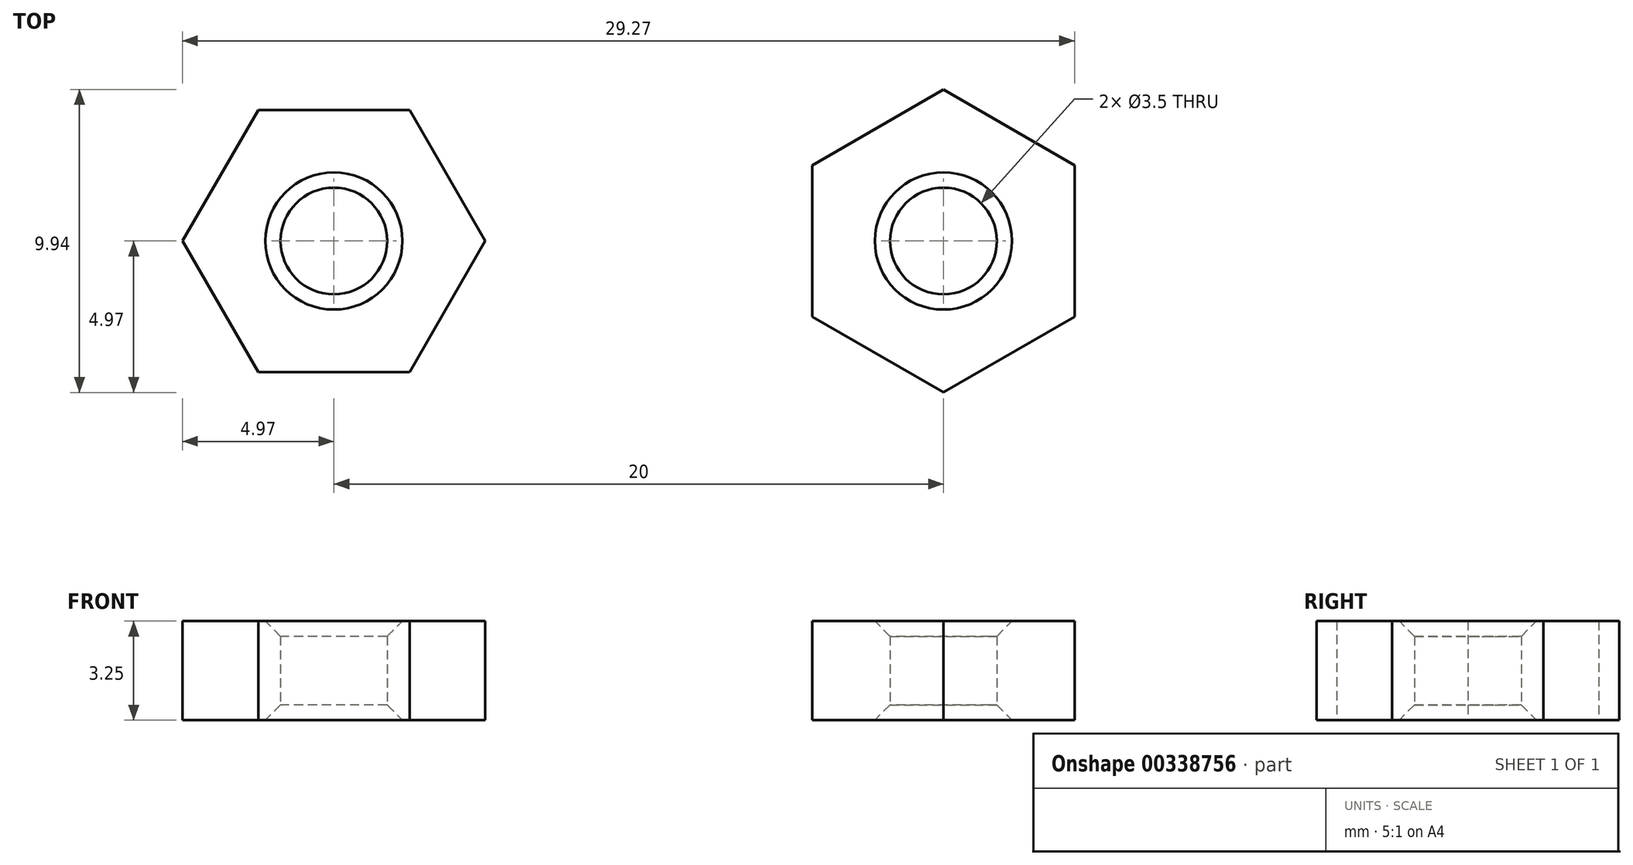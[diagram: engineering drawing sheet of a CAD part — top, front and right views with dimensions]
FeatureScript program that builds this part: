
annotation { "Feature Type Name" : "Feature", "Feature Type Description" : "" }
export const myFeature = defineFeature(function(context is Context, id is Id, definition is map)
    precondition{}
    {
        {
            var Q0;
            Q0=qCreatedBy(makeId("Top.planeOp"),FACE);
            var sketch = newSketch(context, id + "F0", { "sketchPlane" : qUnion([Q0])});
            skCircle(sketch, "E0.cCircle", {"center": v(0, 0) * mm, "radius": 4.3 * mm, "construction": true});
            skLineSegment(sketch, "E0.0", {"start": v(-2.48, 4.3) * mm, "end": v(2.48, 4.3) * mm});
            skLineSegment(sketch, "E0.1", {"start": v(2.48, 4.3) * mm, "end": v(4.97, 0) * mm});
            skLineSegment(sketch, "E0.2", {"start": v(4.97, 0) * mm, "end": v(2.48, -4.3) * mm});
            skLineSegment(sketch, "E0.3", {"start": v(2.48, -4.3) * mm, "end": v(-2.48, -4.3) * mm});
            skLineSegment(sketch, "E0.4", {"start": v(-2.48, -4.3) * mm, "end": v(-4.97, 0) * mm});
            skLineSegment(sketch, "E0.5", {"start": v(-4.97, 0) * mm, "end": v(-2.48, 4.3) * mm});
            skPoint(sketch, "E0.0.midPoint", {"position": v(0, 4.3) * mm});
            skCircle(sketch, "E1", {"center": v(0, 0) * mm, "radius": 1.75 * mm});
            skSolve(sketch);
        }
        {
            var Q0;
            Q0=makeQuery(id+"F0.imprint","IMPRINT",FACE,{"disambiguationData":[TD([[makeQuery(id+"F0.imprint","IMPRINT",EDGE,{"derivedFrom":sQuery(id+"F0.wireOp",EDGE,"E0.0")}),-1.0]])]});
            extrude(context, id + "F1", {"entities" : qUnion([Q0]), "depth" : 3.25 * mm});
        }
        {
            var Q0;
            Q0=makeQuery(id+"F1.opExtrude","CAP_EDGE",EDGE,{"disambiguationData":[OSD([sQuery(id+"F0.wireOp",EDGE,"E1")])],"isStart":false});
            var Q1;
            Q1=makeQuery(id+"F1.opExtrude","CAP_EDGE",EDGE,{"disambiguationData":[OSD([sQuery(id+"F0.wireOp",EDGE,"E1")])],"isStart":true});
            chamfer(context, id + "F2", {"entities" : qUnion([Q0, Q1]), "width" : .5 * mm, "tangentPropagation" : true});
        }
        {
            var Q0;
            Q0=makeQuery(id+"F1.opExtrude","SWEPT_BODY",BODY,{"disambiguationData":[OSD([sQuery(id+"F0.wireOp",EDGE,"E0.0"),sQuery(id+"F0.wireOp",EDGE,"E0.1"),sQuery(id+"F0.wireOp",EDGE,"E0.2"),sQuery(id+"F0.wireOp",EDGE,"E0.3"),sQuery(id+"F0.wireOp",EDGE,"E0.4"),sQuery(id+"F0.wireOp",EDGE,"E0.5"),sQuery(id+"F0.wireOp",EDGE,"E1")])]});
            transform(context, id + "F3", {"entities" : qUnion([Q0]), "transformType" : TransformType.TRANSLATION_3D, "dx" : 20 * mm, "dy" : 0 * mm, "dz" : 0 * mm, "makeCopy" : true});
        }
        {
            var Q0;
            Q0=qCreatedBy(makeId("Front.planeOp"),FACE);
            var sketch = newSketch(context, id + "F4", { "sketchPlane" : qUnion([Q0])});
            skLineSegment(sketch, "E2.0", {"start": v(22.48, 3.25) * mm, "end": v(17.52, 3.25) * mm});
            skLineSegment(sketch, "E3", {"start": v(20, 3.25) * mm, "end": v(20, 8.8) * mm});
            skSolve(sketch);
        }
        {
            var Q0;
            Q0=makeQuery(id+"F3.opPattern","COPY",BODY,{"derivedFrom":makeQuery(id+"F1.opExtrude","SWEPT_BODY",BODY,{"disambiguationData":[OSD([sQuery(id+"F0.wireOp",EDGE,"E0.0"),sQuery(id+"F0.wireOp",EDGE,"E0.1"),sQuery(id+"F0.wireOp",EDGE,"E0.2"),sQuery(id+"F0.wireOp",EDGE,"E0.3"),sQuery(id+"F0.wireOp",EDGE,"E0.4"),sQuery(id+"F0.wireOp",EDGE,"E0.5"),sQuery(id+"F0.wireOp",EDGE,"E1")])]}),"instanceName":"1"});
            var Q1;
            Q1=sQuery(id+"F4.wireOp",EDGE,"E3");
            transform(context, id + "F5", {"entities" : qUnion([Q0]), "transformType" : TransformType.ROTATION, "transformAxis" : qUnion([Q1]), "angle" : 30 * degree, "makeCopy" : false});
        }
    });
